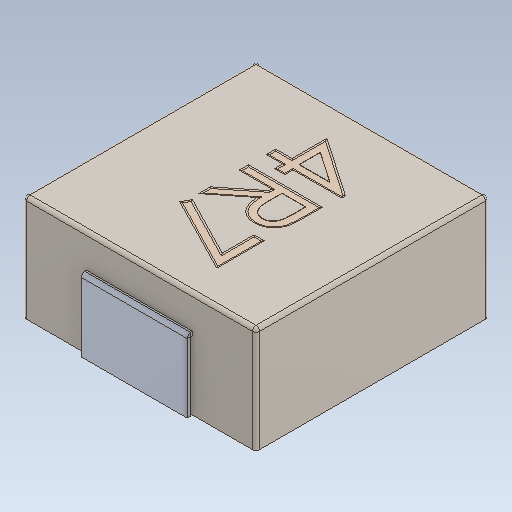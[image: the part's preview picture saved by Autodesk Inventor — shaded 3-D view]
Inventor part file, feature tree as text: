
AUTODESK INVENTOR PART (.ipt)
format: ipt  version: 2020 (Build 240168000, 168)  size: 180,224 bytes
history: native  units: in
note: dims shown in document units (in); Inventor stores cm internally (conversion verified against a paired STEP export)
features: fillet x1
ambient origin geometry x8: Origin, YZ Plane, XZ Plane, XY Plane, X Axis, Y Axis, Z Axis, Center Point
bodies: Solid1 (feature_tree)
feature tree (1):
  fillet  "Fillet2"  [1 undecoded]
note: 1 required parameter value undecoded (feature->parameter linkage not recoverable at this tier; creation-order binding heuristic only, values carry confidence <= 0.55)
